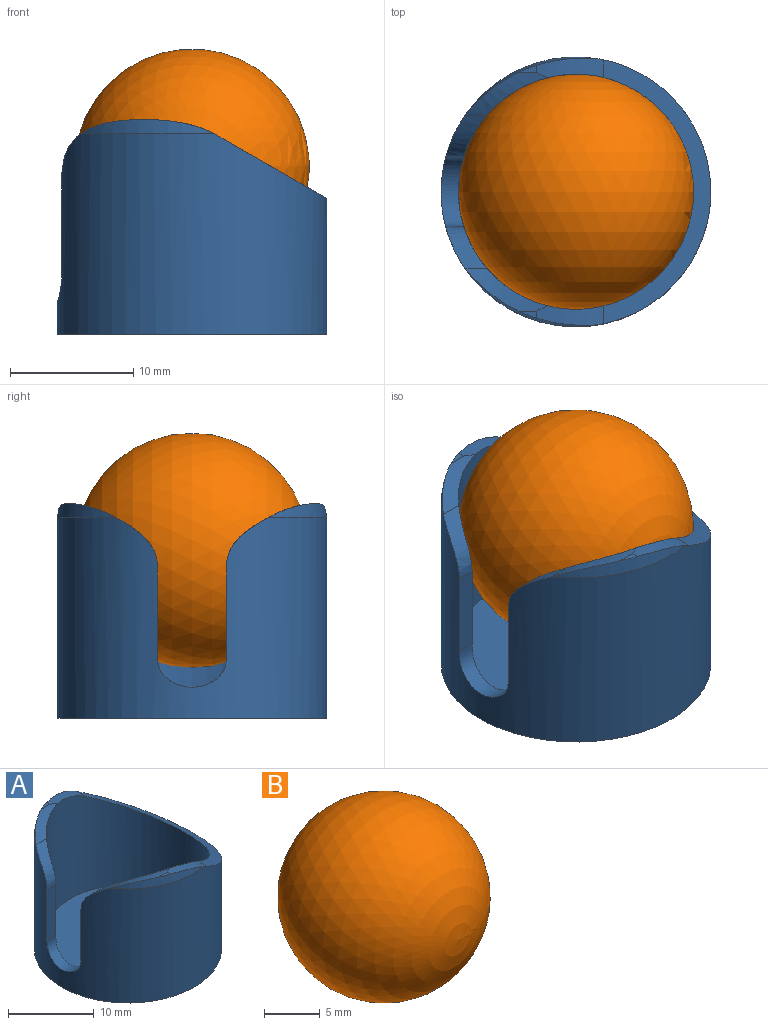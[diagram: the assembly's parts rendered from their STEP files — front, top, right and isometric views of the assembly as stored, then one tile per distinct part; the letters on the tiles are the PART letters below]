
ASSEMBLY  parts=2 mates=1
PART A: 22 faces, bbox 23.7x23.7x19.3 mm
  f0: plane 1.47x0.58mm, normal (0,0,1), area 0.5mm2, adj f2,f7,f16
  f1: extruded ~5.44x1.58mm, area 7.1mm2, adj f4,f8,f9,f11,f12,f15
  f2: extruded ~5.44x1.58mm, area 7.1mm2, adj f0,f4,f7,f8,f12,f16
  f3: extruded ~1.8x0.97mm, area 0mm2, adj f8,f19
  f4: cylinder r=9.52mm len=19.04mm, axis (0,0,1), area 689.2mm2, adj f1,f2,f12,f14,f15,f16,f17,f18
  f5: cylinder r=1.21mm len=2.41mm, axis (0,0,-1), area 18.2mm2, adj f10,f14
  f6: cylinder r=1.21mm len=2.41mm, axis (0,0,-1), area 18.2mm2, adj f10,f14
  f7: cone r=10.72mm half-angle=10deg, axis (0,0,-1), area 10mm2, adj f0,f2,f8,f16
  f8: cylinder r=10.92mm len=21.84mm, axis (0,0,-1), area 928.9mm2, adj f1,f2,f3,f7,f10,f11,f12,f13
  f9: plane 1.47x0.58mm, normal (0,0,1), area 0.5mm2, adj f1,f11,f15
  f10: plane 21.84x21.84mm, normal (0,0,-1), area 365.6mm2, adj f5,f6,f8
  f11: cone r=10.72mm half-angle=10deg, axis (0,0,-1), area 8.9mm2, adj f1,f8,f9,f15
  f12: plane 23.23x10.52mm, normal (0.5,0,0.87), area 44.5mm2, adj f1,f2,f4,f8
  f13: extruded ~1.63x0.46mm, area 0mm2, adj f8,f19
  f14: plane 19.04x19.04mm, normal (0,0,1), area 275.7mm2, adj f4,f5,f6
  f15: extruded ~6.68x3.47mm, area 9.1mm2, adj f1,f4,f9,f11,f17
  f16: extruded ~6.68x3.47mm, area 7.8mm2, adj f0,f2,f4,f7,f21
  f17: extruded ~3.91x3.39mm, area 8.8mm2, adj f4,f8,f15,f18
  f18: plane 7.18x1.46mm, normal (0,1,0), area 10.5mm2, adj f4,f8,f17,f19
  f19: extruded ~5.61x2.65mm, area 14.2mm2, adj f3,f4,f8,f13,f18,f20
  f20: plane 7.18x1.46mm, normal (0,-1,0), area 10.5mm2, adj f4,f8,f19,f21
  f21: extruded ~3.91x3.39mm, area 8.8mm2, adj f4,f8,f16,f20
PART B: 1 faces, bbox 19x19x19 mm
  f0: sphere r=9.5mm, area 1134.1mm2
PLACE A t=(-4,2.79,-1.04)mm fixed
PLACE B t=(-4,2.79,-1.04)mm
MATE fastened B.f0 <-> A.f4  axis (0,0,1) through (-4,2.79,12.57)mm
